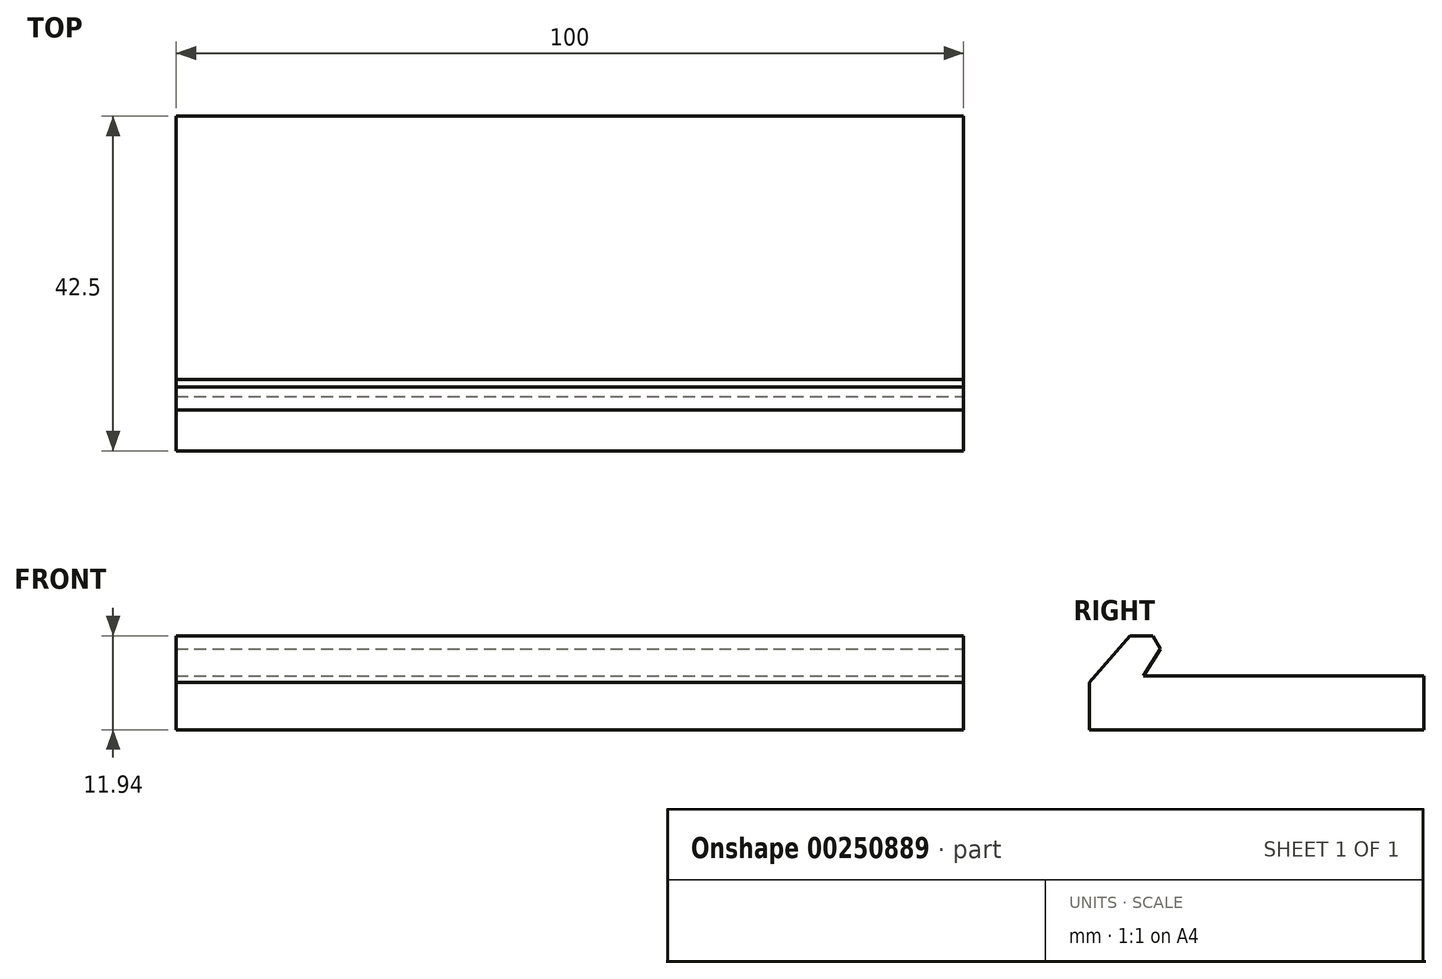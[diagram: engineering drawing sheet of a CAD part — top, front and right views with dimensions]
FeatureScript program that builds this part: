
annotation { "Feature Type Name" : "Feature", "Feature Type Description" : "" }
export const myFeature = defineFeature(function(context is Context, id is Id, definition is map)
    precondition{}
    {
        {
            var Q0;
            Q0=qCreatedBy(makeId("Top.planeOp"),FACE);
            var sketch = newSketch(context, id + "F0", { "sketchPlane" : qUnion([Q0])});
            skLineSegment(sketch, "E0.bottom", {"start": v(45, -25) * mm, "end": v(-45, -25) * mm});
            skLineSegment(sketch, "E0.top", {"start": v(47.5, 25) * mm, "end": v(-47.5, 25) * mm});
            skLineSegment(sketch, "E0.left", {"start": v(50, -20) * mm, "end": v(50, 22.5) * mm});
            skLineSegment(sketch, "E0.right", {"start": v(-50, -20) * mm, "end": v(-50, 22.5) * mm});
            skPoint(sketch, "E0.middle", {"position": v(0, 0) * mm});
            skArc(sketch, "E1", {"start": v(-47.5, 25) * mm, "mid": v(-49.27, 24.27) * mm, "end": v(-50, 22.5) * mm});
            skPoint(sketch, "E2.orphan", {"position": v(-50, 25) * mm});
            skArc(sketch, "E3", {"start": v(50, 22.5) * mm, "mid": v(49.27, 24.27) * mm, "end": v(47.5, 25) * mm});
            skPoint(sketch, "E4.orphan", {"position": v(50, 25) * mm});
            skPoint(sketch, "E5.visualSharp", {"position": v(-50, -25) * mm});
            skArc(sketch, "E5.filletArc", {"start": v(-50, -20) * mm, "mid": v(-48.54, -23.54) * mm, "end": v(-45, -25) * mm});
            skPoint(sketch, "E6.visualSharp", {"position": v(50, -25) * mm});
            skArc(sketch, "E6.filletArc", {"start": v(45, -25) * mm, "mid": v(48.54, -23.54) * mm, "end": v(50, -20) * mm});
            skSolve(sketch);
        }
        {
            var Q0;
            Q0 = qSketchRegion(id + "F0", true);
            extrude(context, id + "F1", {"entities" : qUnion([Q0]), "depth" : 25 * mm});
        }
        {
            var Q0;
            Q0=makeQuery(id+"F1.opExtrude","SWEPT_FACE",FACE,{"disambiguationData":[OSD([sQuery(id+"F0.wireOp",EDGE,"E0.left")])]});
            var sketch = newSketch(context, id + "F2", { "sketchPlane" : qUnion([Q0])});
            skLineSegment(sketch, "E7", {"start": v(25.47, 0) * mm, "end": v(-25.22, 0) * mm});
            skLineSegment(sketch, "E8", {"start": v(-25.22, 0) * mm, "end": v(-14.85, 11.94) * mm});
            skLineSegment(sketch, "E9", {"start": v(-14.85, 11.94) * mm, "end": v(-11.91, 11.94) * mm});
            skLineSegment(sketch, "E10", {"start": v(-11.91, 11.94) * mm, "end": v(-10.96, 10.25) * mm});
            skLineSegment(sketch, "E11", {"start": v(-10.96, 10.25) * mm, "end": v(-13.13, 6.84) * mm});
            skLineSegment(sketch, "E12", {"start": v(-13.13, 6.84) * mm, "end": v(25.09, 6.84) * mm});
            skLineSegment(sketch, "E13", {"start": v(25.09, 6.84) * mm, "end": v(25.47, 0) * mm});
            skLineSegment(sketch, "E14", {"start": v(25.47, 0) * mm, "end": v(36.33, 11.94) * mm});
            skLineSegment(sketch, "E15", {"start": v(36.33, 11.94) * mm, "end": v(27.17, 33.98) * mm});
            skLineSegment(sketch, "E16", {"start": v(27.17, 33.98) * mm, "end": v(-13.13, 31.71) * mm});
            skLineSegment(sketch, "E17", {"start": v(-13.13, 31.71) * mm, "end": v(-32.78, 29.16) * mm});
            skLineSegment(sketch, "E18", {"start": v(-32.78, 29.16) * mm, "end": v(-25.22, 0) * mm});
            skSolve(sketch);
        }
        {
            var Q0;
            {var subQ3=sQuery(id+"F2.wireOp",EDGE,"E13");Q0=makeQuery(id+"F2.imprint","IMPRINT",FACE,{"disambiguationData":[TD([[makeQuery(id+"F2.imprint","IMPRINT",EDGE,{"derivedFrom":subQ3}),-1.0]])]});}
            var Q1;
            {var subQ0=sQuery(id+"F2.wireOp",EDGE,"E7");var subQ1=makeQuery(id+"F1.opExtrude","SWEPT_EDGE",EDGE,{"disambiguationData":[OSD([sQuery(id+"F0.wireOp",EDGE,"E0.left"),sQuery(id+"F0.wireOp",EDGE,"E6.filletArc")])]});var subQ2=makeQuery(id+"F2.imprint","INTERSECT",VERTEX,{"derivedFrom":[subQ1,subQ0]});var subQ3=sQuery(id+"F2.wireOp",EDGE,"E8");var subQ4=makeQuery(id+"F2.imprint","INTERSECT",VERTEX,{"derivedFrom":[subQ0,subQ3,sQuery(id+"F2.wireOp",EDGE,"E18")]});Q1=makeQuery(id+"F2.imprint","IMPRINT",FACE,{"disambiguationData":[TD([[makeQuery(id+"F2.imprint","IMPRINT",EDGE,{"disambiguationData":[TD([[subQ2,-1.0],[subQ4,1.0]])],"derivedFrom":subQ0}),-1.0]])]});}
            var Q2;
            {var subQ6=sQuery(id+"F2.wireOp",EDGE,"E9");Q2=makeQuery(id+"F2.imprint","IMPRINT",FACE,{"disambiguationData":[TD([[makeQuery(id+"F2.imprint","IMPRINT",EDGE,{"derivedFrom":subQ6}),1.0]])]});}
            var Q3;
            {var subQ6=sQuery(id+"F2.wireOp",EDGE,"E13");Q3=makeQuery(id+"F2.imprint","IMPRINT",FACE,{"disambiguationData":[TD([[makeQuery(id+"F2.imprint","IMPRINT",EDGE,{"derivedFrom":subQ6}),1.0]])]});}
            extrude(context, id + "F3", {"entities" : qUnion([Q0, Q1, Q2, Q3]), "operationType" : NewBodyOperationType.REMOVE, "oppositeDirection" : true, "depth" : 106.1 * mm});
        }
    });
